# Revit family: Schmutzfänger 4111
name_source: partatom
category: Rohrzubehör
units: mm (PartAtom-declared; Revit-internal decimal feet)

## family parameters
Arbeitsebenenbasiert = Nein
Beim Laden mit Abzugskörper schneiden = Nein
Bemaßung runder Anschluss = Durchmesser verwenden
Gemeinsam genutzt = Nein
Immer vertikal = Ja
OmniClass-Nummer = 23.65.55.14
OmniClass-Titel = Valves for Liquid Services
Teiletyp = Unterbricht

## types (1)
- Schmutzfänger 4111
    Anwendungsgebiet = Die Schmutzfänger werden in Rohrleitungen eingebaut, um schädliche Fremdkörper von den feinst bearbeiteten
Ventilsitzen fernzuhalten. Anwendungsgebiete sind haustechnische Anlagen, wie z.B. Heizungs- oder
Kaltwasseranlagen für die Klimatisierung von Gebäuden. Aromatische Chlorkohlenwasserstoffe, welche in Erdgas,
Erdölen und Schmiermitteln vorkommen, zerstören die EPDM- Dichtungen.
    Dichtungen = EPDM
    Gehäuse = entzinkungsbeständiges Messing CC770S
    Hersteller = Herz-Armaturen GmbH
    Innengewinde = gem. ISO 228-1
    L03 = 15 mm
    L10 = 3.5 mm  [stored 0.0114829 ft]
    L12 = 0.8 mm
    Medium = Heizungswasserqualität nach ÖNORM H 5195 oder VDI-Richtline 2035. Die Verwendung von Ethylen- oder
Propylenglykol in einem Mischungsverhältnis 25 - 50% ist zulässig. Bitte beachten Sie die Hersteller- Dokumentation,
wenn Glykol-Produkte für Frost- und Korrosionsschutz zum Einsatz kommen. EPDM-Dichtungen können durch
Mineralöle und Schmiermittel beschädigt werden und somit kann es zum Versagen der EPDM-Dichtungen führen.
HERZ Kugelhähne sind nicht für den Einsatz von agressiven Medien (wie Säuren, Laugen, brennbaren und explosiven
Gase) geeignet, da die Dichtelemente beschädigt werden können.
    R03 = 9.5 mm
    R100 = 1 mm  [stored 0.00328084 ft]
    SCRNCODE = 05;15;02
    SCRNSEQ = AWI;AWI_TYP="1011";2
    SCTWCODE = 04;16;02
    SCTWSEQ = AW;SBT_TYP_AW="112";2
    Sieb = Streckmetall, Rautenmasche, Edelstahl 1.4301, Maschenweite 0,75mm
    Siebkappe = geschmiedetes Messing gem. EN 12420, CW617N
    URL = www.herz-armaturen.at
    Vorgabe-Ansicht = 0 mm  [stored 0 ft]
    W01 = 45.00°
    max.Betriebstemp. = 110 °C

note: [stored X ft] marks values corroborated as IEEE doubles in the binary element streams (Revit-internal decimal feet)
